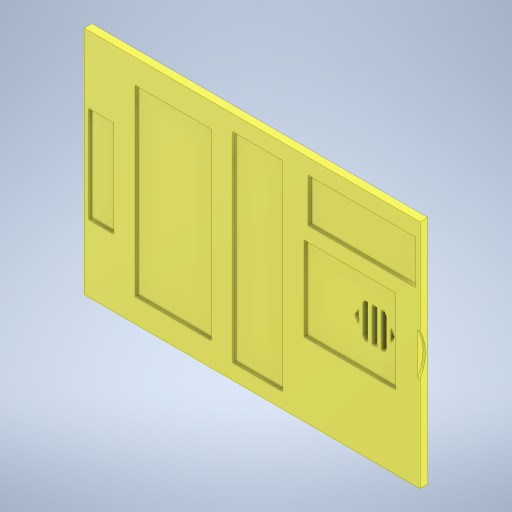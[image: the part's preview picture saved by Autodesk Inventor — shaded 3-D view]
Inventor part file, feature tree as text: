
AUTODESK INVENTOR PART (.ipt)
format: ipt  version: 2023 (Build 270158030, 158C)  size: 559,616 bytes
history: native  units: mm
features: sketch x16, extrude x15, hole x3, mirror x1, projected_geometry x1
ambient origin geometry x8: Origin, YZ Plane, XZ Plane, XY Plane, X Axis, Y Axis, Z Axis, Center Point
bodies: Solid1 (feature_tree)
feature tree (36):
  extrude  "MainInnerBodyExtrusion"  Depth=149.0mm
  extrude  "HoleForCamerabase"  Depth=15.7mm
  extrude  "HoleForFan"  Depth=59.0mm
  extrude  "HoleForPi"  TaperAngle=0.0deg  [1 undecoded]
  extrude  "HoleForPoeAdapter"  Depth=62.0mm
  extrude  "HoleForThermister"  Depth=47.0mm
  extrude  "HoleForSensor"  Depth=32.0mm
  extrude  "SlotsForRearFan"  Depth=47.0mm
  extrude  "VentForCamera"  Depth=14.0mm
  extrude  "HoleForLens"  Depth=118.0mm
  sketch  "Sketch23"  dims[d26=49.0mm d27=118.0mm]
  hole  "Hole for 6-32 Insert"  [1 undecoded]
  hole  "Screw hole for 6-32 screw"  [1 undecoded]
  hole  "Side hole for 1-4 20 insert"  [1 undecoded]
  mirror  "Mirror for side insert"
  extrude  "Extrusion18"  Depth=17.0mm
  extrude  "Extrusion19"  TaperAngle=0.0deg  [1 undecoded]
  extrude  "Extrusion20"  Depth=2.0mm
  extrude  "Extrusion21"  Depth=4.0mm
  extrude  "Extrusion22"  Depth=4.0mm
  sketch  "Sketch1"  dims[d0=216.7mm d1=149.0mm]
  sketch  "Sketch3"  dims[d2=50.0mm d3=0.0mm d5=15.7mm]
  sketch  "Sketch4"  dims[d6=54.0mm d7=59.0mm]
  sketch  "Sketch6"  dims[d8=47.0mm d9=0.0mm]
  sketch  "Sketch7"  dims[d13=16.0mm d14=62.0mm]
  sketch  "Sketch11"  dims[d15=3.0mm d16=47.0mm]
  sketch  "Sketch15"  dims[d17=0.0mm d20=32.0mm]
  sketch  "Sketch16"  dims[d21=129.0mm d22=47.0mm]
  sketch  "Sketch18"  dims[d23=0.0mm d25=14.0mm]
  sketch  "Sketch24"  dims[d28=47.0mm d29=0.0mm]
  sketch  "Sketch25"  dims[d36=69.0mm d37=28.0mm]
  projected_geometry  "Projected Loop1"
  sketch  "Sketch26"  dims[d38=47.0mm d39=0.0mm]
  sketch  "Sketch30"  dims[d42=50.0mm d43=17.0mm]
  sketch  "Sketch35"  dims[d46=31.5mm d47=0.0mm]
  sketch  "Sketch36"  dims[d67=60.0mm d69=2.0mm d71=4.0mm d72=4.0mm d73=4.0mm d75=4.0mm d76=10.0mm d77=0.0mm d78=15.5mm d79=22.0mm d85=3.0mm d86=3.0mm d87=10.0mm d88=14.0mm d89=1.5mm d90=3.0mm d91=3.0mm d92=3.0mm d93=0.0mm d94=0.0mm d95=15.0mm d97=16.0mm d98=10.0mm d99=0.0mm d106=5.0mm d108=5.0mm d109=4.7mm d110=6.0mm d111=5.54mm d112=5.55mm d113=90.0deg d114=7.2mm d115=20.594885mm d116=3.797mm d117=6.0mm d118=12.7mm d119=2.362mm d120=90.0deg d121=15.0mm d122=20.594885mm d130=7.666mm d131=6.0mm d132=8.406mm d133=7.41mm d134=90.0deg d135=9.53mm d136=20.594885mm d137=24.0mm d138=10.0mm d139=3.0mm d140=25.0mm d141=0.0mm d142=30.0mm d144=10.0mm d145=0.0mm d162=55.0mm d163=29.0mm d164=46.0mm d165=21.0mm d166=1.5mm d167=0.0mm d215=4.8514mm d216=5.0mm d217=5.0mm d218=10.0mm d219=10.0mm d220=9.525mm d221=0.0mm d222=76.2mm d223=76.2mm d224=76.2mm d225=76.2mm d226=25.0mm d227=108.350001mm d228=45.0mm d229=0.0mm d230=0.0mm]
note: 5 required parameter values undecoded (feature->parameter linkage not recoverable at this tier; creation-order binding heuristic only, values carry confidence <= 0.55)
